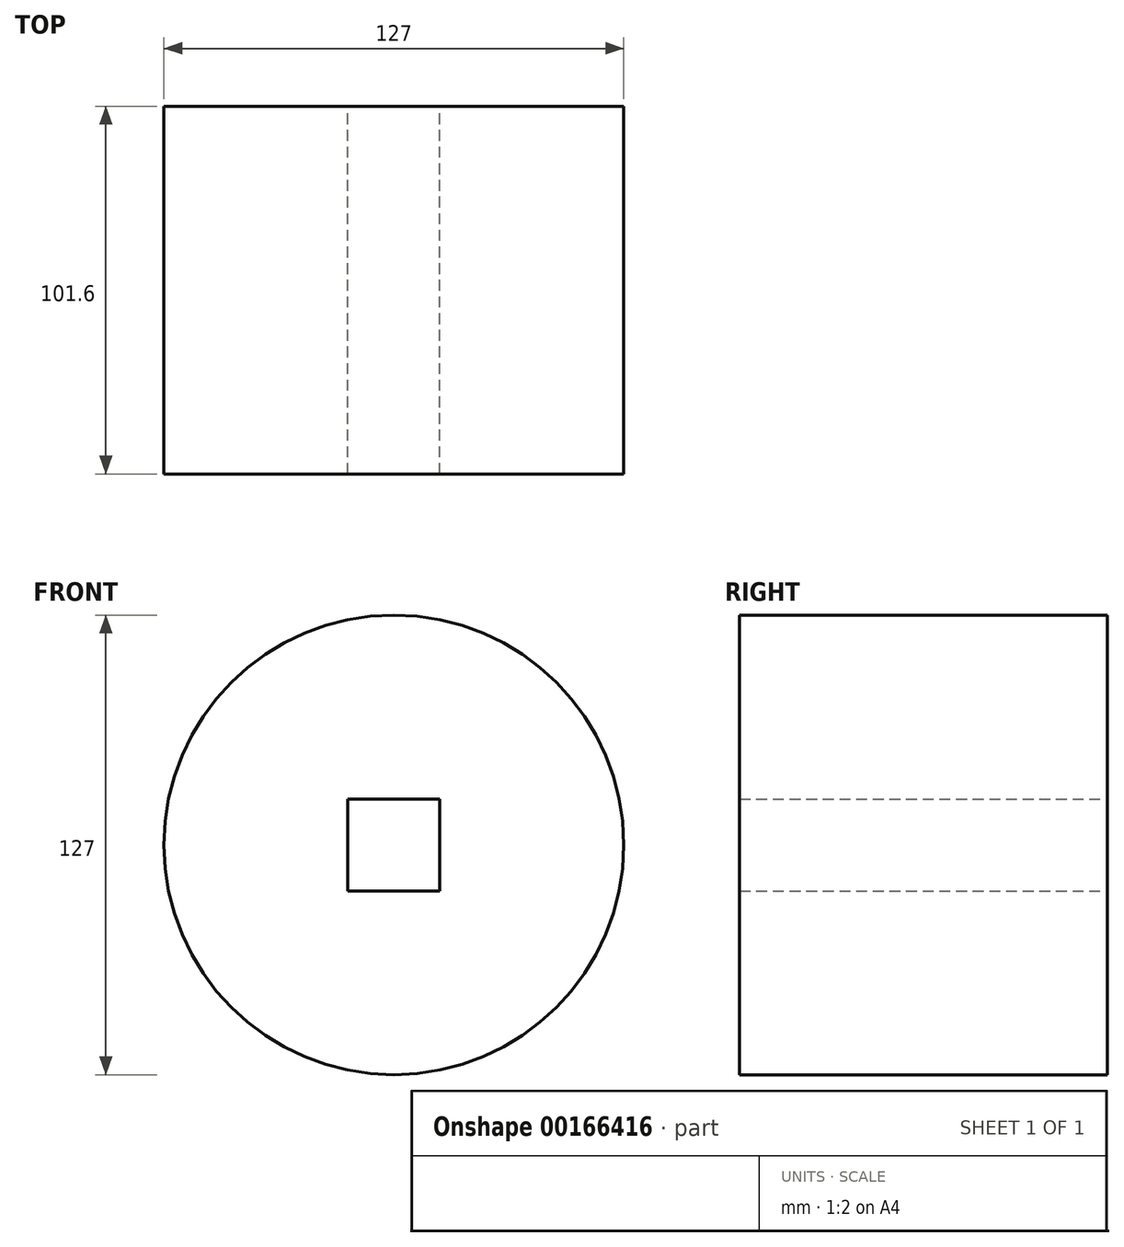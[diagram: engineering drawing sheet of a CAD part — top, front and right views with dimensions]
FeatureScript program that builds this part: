
annotation { "Feature Type Name" : "Feature", "Feature Type Description" : "" }
export const myFeature = defineFeature(function(context is Context, id is Id, definition is map)
    precondition{}
    {
        {
            var Q0;
            Q0=qCreatedBy(makeId("Front.planeOp"),FACE);
            var sketch = newSketch(context, id + "F0", { "sketchPlane" : qUnion([Q0])});
            skCircle(sketch, "E0", {"center": v(0, 0) * mm, "radius": 63.5 * mm});
            skLineSegment(sketch, "E1.bottom", {"start": v(12.7, 12.7) * mm, "end": v(-12.7, 12.7) * mm});
            skLineSegment(sketch, "E1.top", {"start": v(12.7, -12.7) * mm, "end": v(-12.7, -12.7) * mm});
            skLineSegment(sketch, "E1.left", {"start": v(12.7, 12.7) * mm, "end": v(12.7, -12.7) * mm});
            skLineSegment(sketch, "E1.right", {"start": v(-12.7, 12.7) * mm, "end": v(-12.7, -12.7) * mm});
            skSolve(sketch);
        }
        {
            var Q0;
            Q0=makeQuery(id+"F0.imprint","IMPRINT",FACE,{"disambiguationData":[TD([[makeQuery(id+"F0.imprint","IMPRINT",EDGE,{"derivedFrom":sQuery(id+"F0.wireOp",EDGE,"E0")}),1.0]])]});
            extrude(context, id + "F1", {"entities" : qUnion([Q0]), "depth" : 50.8 * mm});
        }
        {
            var Q0;
            Q0 = qSketchRegion(id + "F0", true);
            extrude(context, id + "F2", {"entities" : qUnion([Q0]), "operationType" : NewBodyOperationType.ADD, "oppositeDirection" : true, "depth" : 50.8 * mm});
        }
    });
